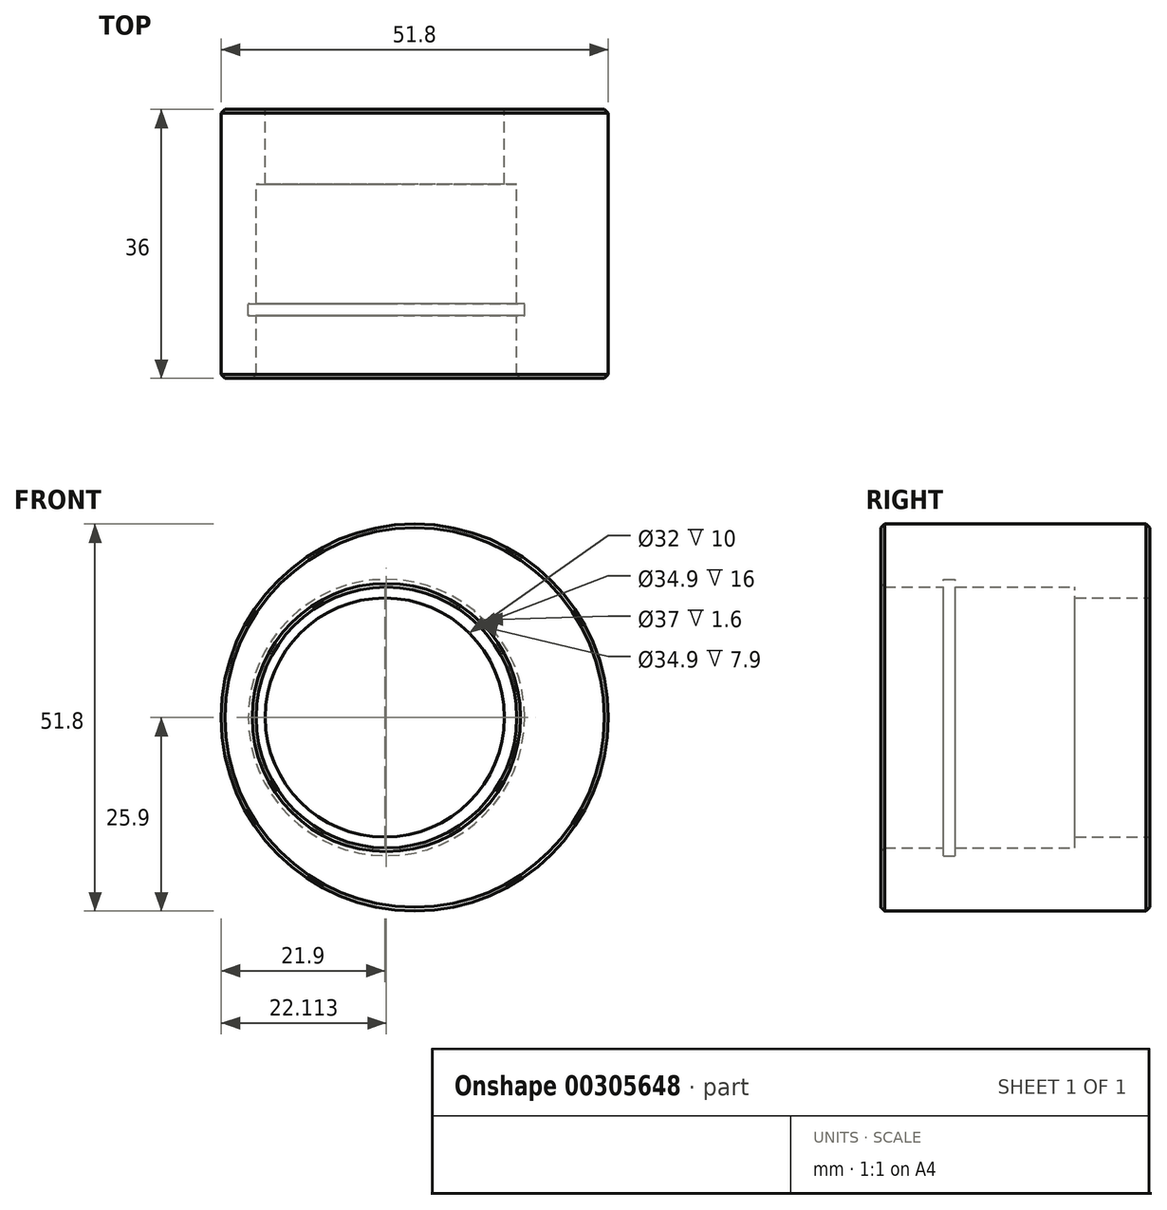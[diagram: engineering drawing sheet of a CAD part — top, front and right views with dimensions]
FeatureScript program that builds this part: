
annotation { "Feature Type Name" : "Feature", "Feature Type Description" : "" }
export const myFeature = defineFeature(function(context is Context, id is Id, definition is map)
    precondition{}
    {
        {
            var Q0;
            Q0=qCreatedBy(makeId("Front.planeOp"),FACE);
            var sketch = newSketch(context, id + "F0", { "sketchPlane" : qUnion([Q0])});
            skCircle(sketch, "E0", {"center": v(0, 0) * mm, "radius": 25.9 * mm});
            skCircle(sketch, "E1", {"center": v(-4, 0) * mm, "radius": 16 * mm});
            skSolve(sketch);
        }
        {
            var Q0;
            Q0=makeQuery(id+"F0.imprint","IMPRINT",FACE,{"disambiguationData":[TD([[makeQuery(id+"F0.imprint","IMPRINT",EDGE,{"derivedFrom":sQuery(id+"F0.wireOp",EDGE,"E0")}),1.0]])]});
            var Q1;
            Q1=makeQuery(id+"F0.imprint","IMPRINT",FACE,{"disambiguationData":[TD([[makeQuery(id+"F0.imprint","IMPRINT",EDGE,{"derivedFrom":sQuery(id+"F0.wireOp",EDGE,"T585qWjt-wNxM-GuRu-T1lm-ynMxdenTDOOd")}),1.0]])]});
            extrude(context, id + "F1", {"entities" : qUnion([Q0, Q1]), "depth" : 10 * mm});
        }
        {
            var Q0;
            Q0=makeQuery(id+"F1.opExtrude","CAP_FACE",FACE,{"disambiguationData":[OSD([sQuery(id+"F0.wireOp",EDGE,"E0"),sQuery(id+"F0.wireOp",EDGE,"E1")])],"isStart":false});
            var sketch = newSketch(context, id + "F2", { "sketchPlane" : qUnion([Q0])});
            skLineSegment(sketch, "E2", {"start": v(0, 0) * mm, "end": v(-4, 0) * mm});
            skSolve(sketch);
        }
        {
            var Q0;
            Q0=makeQuery(id+"F2.imprint","IMPRINT",FACE,{"disambiguationData":[TD([[makeQuery(id+"F2.imprint","IMPRINT",EDGE,{"derivedFrom":makeQuery(id+"F1.opExtrude","CAP_EDGE",EDGE,{"disambiguationData":[OSD([sQuery(id+"F0.wireOp",EDGE,"E0")])],"isStart":false})}),1.0]])]});
            var sketch = newSketch(context, id + "F3", { "sketchPlane" : qUnion([Q0])});
            skCircle(sketch, "E3", {"center": v(-3.79, 0) * mm, "radius": 17.45 * mm});
            skSolve(sketch);
        }
        {
            var Q0;
            Q0=makeQuery(id+"F3.imprint","IMPRINT",FACE,{"disambiguationData":[TD([[makeQuery(id+"F3.imprint","IMPRINT",EDGE,{"derivedFrom":sQuery(id+"F3.wireOp",EDGE,"E3")}),-1.0]])]});
            extrude(context, id + "F4", {"entities" : qUnion([Q0]), "operationType" : NewBodyOperationType.ADD, "depth" : 16 * mm});
        }
        {
            var Q0;
            Q0=makeQuery(id+"F4.opExtrude","CAP_FACE",FACE,{"disambiguationData":[OSD([sQuery(id+"F0.wireOp",EDGE,"E0"),sQuery(id+"F3.wireOp",EDGE,"E3")])],"isStart":false});
            var sketch = newSketch(context, id + "F5", { "sketchPlane" : qUnion([Q0])});
            skCircle(sketch, "E4", {"center": v(-3.79, 0) * mm, "radius": 18.5 * mm});
            skSolve(sketch);
        }
        {
            var Q0;
            Q0=makeQuery(id+"F5.imprint","IMPRINT",FACE,{"disambiguationData":[TD([[makeQuery(id+"F5.imprint","IMPRINT",EDGE,{"derivedFrom":sQuery(id+"F5.wireOp",EDGE,"E4")}),-1.0]])]});
            extrude(context, id + "F6", {"entities" : qUnion([Q0]), "operationType" : NewBodyOperationType.ADD, "depth" : 1.6 * mm});
        }
        {
            var Q0;
            Q0=makeQuery(id+"F6.opExtrude","CAP_FACE",FACE,{"disambiguationData":[OSD([sQuery(id+"F0.wireOp",EDGE,"E0"),sQuery(id+"F5.wireOp",EDGE,"E4")])],"isStart":false});
            var sketch = newSketch(context, id + "F7", { "sketchPlane" : qUnion([Q0])});
            skCircle(sketch, "E5", {"center": v(-3.79, 0) * mm, "radius": 17.45 * mm});
            skSolve(sketch);
        }
        {
            var Q0;
            Q0=makeQuery(id+"F7.imprint","IMPRINT",FACE,{"disambiguationData":[TD([[makeQuery(id+"F7.imprint","IMPRINT",EDGE,{"derivedFrom":makeQuery(id+"F6.opExtrude","CAP_EDGE",EDGE,{"disambiguationData":[OSD([sQuery(id+"F5.wireOp",EDGE,"E4")])],"isStart":false})}),-1.0]])]});
            var Q1;
            Q1=makeQuery(id+"F7.imprint","IMPRINT",FACE,{"disambiguationData":[TD([[makeQuery(id+"F7.imprint","IMPRINT",EDGE,{"derivedFrom":sQuery(id+"F7.wireOp",EDGE,"E5")}),-1.0]])]});
            extrude(context, id + "F8", {"entities" : qUnion([Q0, Q1]), "operationType" : NewBodyOperationType.ADD, "depth" : 8.4 * mm});
        }
        {
            var Q0;
            Q0=makeQuery(id+"F1.opExtrude","CAP_EDGE",EDGE,{"disambiguationData":[OSD([sQuery(id+"F0.wireOp",EDGE,"E0")])],"isStart":true});
            chamfer(context, id + "F9", {"entities" : qUnion([Q0]), "width" : 0.5 * mm, "tangentPropagation" : true});
        }
        {
            var Q0;
            Q0=makeQuery(id+"F8.opExtrude","CAP_EDGE",EDGE,{"disambiguationData":[OSD([sQuery(id+"F0.wireOp",EDGE,"E0")])],"isStart":false});
            chamfer(context, id + "F10", {"entities" : qUnion([Q0]), "width" : 0.5 * mm, "tangentPropagation" : true});
        }
        {
            var Q0;
            Q0=makeQuery(id+"F8.opExtrude","CAP_EDGE",EDGE,{"disambiguationData":[OSD([sQuery(id+"F7.wireOp",EDGE,"E5")])],"isStart":false});
            chamfer(context, id + "F11", {"entities" : qUnion([Q0]), "width" : 0.5 * mm, "tangentPropagation" : true});
        }
    });
